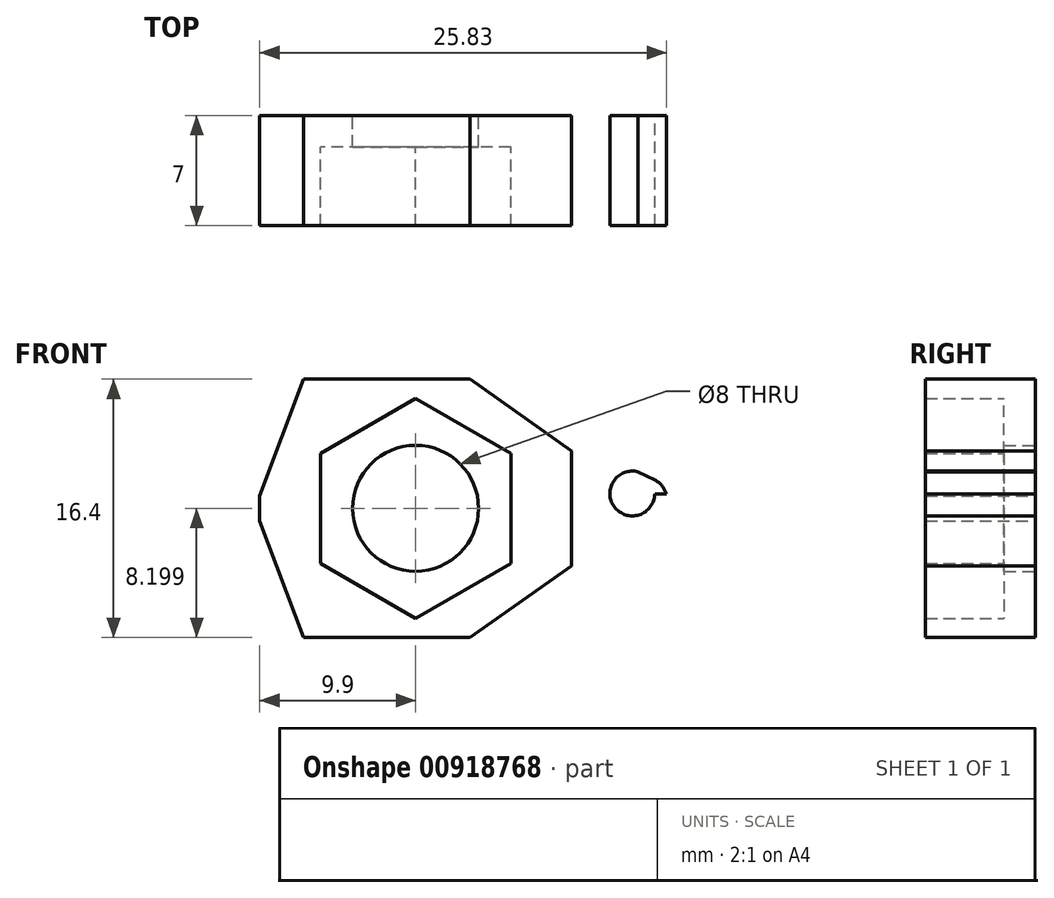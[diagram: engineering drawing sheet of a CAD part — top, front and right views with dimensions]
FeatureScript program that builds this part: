
annotation { "Feature Type Name" : "Feature", "Feature Type Description" : "" }
export const myFeature = defineFeature(function(context is Context, id is Id, definition is map)
    precondition{}
    {
        {
            var Q0;
            Q0=qCreatedBy(makeId("Front.planeOp"),FACE);
            var sketch = newSketch(context, id + "F0", { "sketchPlane" : qUnion([Q0])});
            skLineSegment(sketch, "E0.bottom", {"start": v(-14.42, 4.05) * mm, "end": v(5.38, 4.05) * mm});
            skLineSegment(sketch, "E0.top", {"start": v(-14.42, -12.35) * mm, "end": v(5.38, -12.35) * mm});
            skLineSegment(sketch, "E0.left", {"start": v(-14.42, 4.05) * mm, "end": v(-14.42, -12.35) * mm});
            skLineSegment(sketch, "E0.right", {"start": v(5.38, 4.05) * mm, "end": v(5.38, -12.35) * mm});
            skLineSegment(sketch, "E1", {"start": v(-1.07, 4.05) * mm, "end": v(5.38, -0.5) * mm});
            skLineSegment(sketch, "E2", {"start": v(-1.07, -12.35) * mm, "end": v(5.38, -7.8) * mm});
            skLineSegment(sketch, "E3.bottom", {"start": v(5.38, -0.5) * mm, "end": v(11.38, -0.5) * mm});
            skLineSegment(sketch, "E3.top", {"start": v(5.38, -6.97) * mm, "end": v(11.38, -6.97) * mm});
            skLineSegment(sketch, "E3.left", {"start": v(5.38, -0.5) * mm, "end": v(5.38, -6.97) * mm});
            skLineSegment(sketch, "E3.right", {"start": v(11.46, -3.49) * mm, "end": v(11.46, -3.61) * mm});
            skLineSegment(sketch, "E4", {"start": v(-11.62, 4.05) * mm, "end": v(-14.42, -3.35) * mm});
            skLineSegment(sketch, "E5", {"start": v(-14.42, -4.95) * mm, "end": v(-11.62, -12.35) * mm});
            skCircle(sketch, "E6", {"center": v(9.24, -3.2) * mm, "radius": 1.43 * mm});
            skLineSegment(sketch, "E7", {"start": v(6.93, -0.5) * mm, "end": v(10.68, -2.36) * mm});
            skLineSegment(sketch, "E8", {"start": v(6.93, -6.97) * mm, "end": v(10.77, -4.69) * mm});
            skPoint(sketch, "E9.endSnap0", {"position": v(11.46, -3.25) * mm});
            skLineSegment(sketch, "E10", {"start": v(11.46, -3.25) * mm, "end": v(10.67, -3.25) * mm});
            skPoint(sketch, "E11.newPointB", {"position": v(11.46, -6.9) * mm});
            skArc(sketch, "E11.filletArc", {"start": v(10.77, -4.69) * mm, "mid": v(11.27, -4.18) * mm, "end": v(11.46, -3.49) * mm});
            skPoint(sketch, "E12.newPointB", {"position": v(11.46, 0.41) * mm});
            skArc(sketch, "E12.filletArc", {"start": v(11.46, -3.61) * mm, "mid": v(11.25, -2.88) * mm, "end": v(10.68, -2.36) * mm});
            skCircle(sketch, "E13.cCircle", {"center": v(-4.52, -4.15) * mm, "radius": 6.05 * mm, "construction": true});
            skLineSegment(sketch, "E13.0", {"start": v(1.53, -7.64) * mm, "end": v(-4.52, -11.14) * mm});
            skLineSegment(sketch, "E13.1", {"start": v(-4.52, -11.14) * mm, "end": v(-10.57, -7.64) * mm});
            skLineSegment(sketch, "E13.2", {"start": v(-10.57, -7.64) * mm, "end": v(-10.57, -0.66) * mm});
            skLineSegment(sketch, "E13.3", {"start": v(-10.57, -0.66) * mm, "end": v(-4.52, 2.84) * mm});
            skLineSegment(sketch, "E13.4", {"start": v(-4.52, 2.84) * mm, "end": v(1.53, -0.66) * mm});
            skLineSegment(sketch, "E13.5", {"start": v(1.53, -0.66) * mm, "end": v(1.53, -7.64) * mm});
            skPoint(sketch, "E13.0.midPoint", {"position": v(-1.5, -9.4) * mm});
            skCircle(sketch, "E14", {"center": v(-4.52, -4.15) * mm, "radius": 4 * mm});
            skSolve(sketch);
        }
        {
            var Q0;
            {var subQ6=sQuery(id+"F0.wireOp",EDGE,"E1");Q0=makeQuery(id+"F0.imprint","IMPRINT",FACE,{"disambiguationData":[TD([[makeQuery(id+"F0.imprint","IMPRINT",EDGE,{"derivedFrom":subQ6}),-1.0]])]});}
            var Q1;
            Q1=makeQuery(id+"F0.imprint","IMPRINT",FACE,{"disambiguationData":[TD([[makeQuery(id+"F0.imprint","IMPRINT",EDGE,{"derivedFrom":sQuery(id+"F0.wireOp",EDGE,"E6")}),-1.0]])]});
            var Q2;
            Q2=makeQuery(id+"F0.imprint","IMPRINT",FACE,{"disambiguationData":[TD([[makeQuery(id+"F0.imprint","IMPRINT",EDGE,{"derivedFrom":sQuery(id+"F0.wireOp",EDGE,"E6")}),1.0]])]});
            var Q3;
            {var subQ5=sQuery(id+"F0.wireOp",EDGE,"E3.left");Q3=makeQuery(id+"F0.imprint","IMPRINT",FACE,{"disambiguationData":[TD([[makeQuery(id+"F0.imprint","IMPRINT",EDGE,{"derivedFrom":subQ5}),1.0]])]});}
            extrude(context, id + "F1", {"entities" : qUnion([Q0, Q1, Q2, Q3]), "depth" : 7 * mm, "offsetDistance" : 25 * mm});
        }
        {
            var Q0;
            Q0=makeQuery(id+"F0.imprint","IMPRINT",FACE,{"disambiguationData":[TD([[makeQuery(id+"F0.imprint","IMPRINT",EDGE,{"derivedFrom":sQuery(id+"F0.wireOp",EDGE,"E13.0")}),-1.0]])]});
            extrude(context, id + "F2", {"entities" : qUnion([Q0]), "operationType" : NewBodyOperationType.ADD, "depth" : 2 * mm, "offsetDistance" : 25 * mm});
        }
    });
